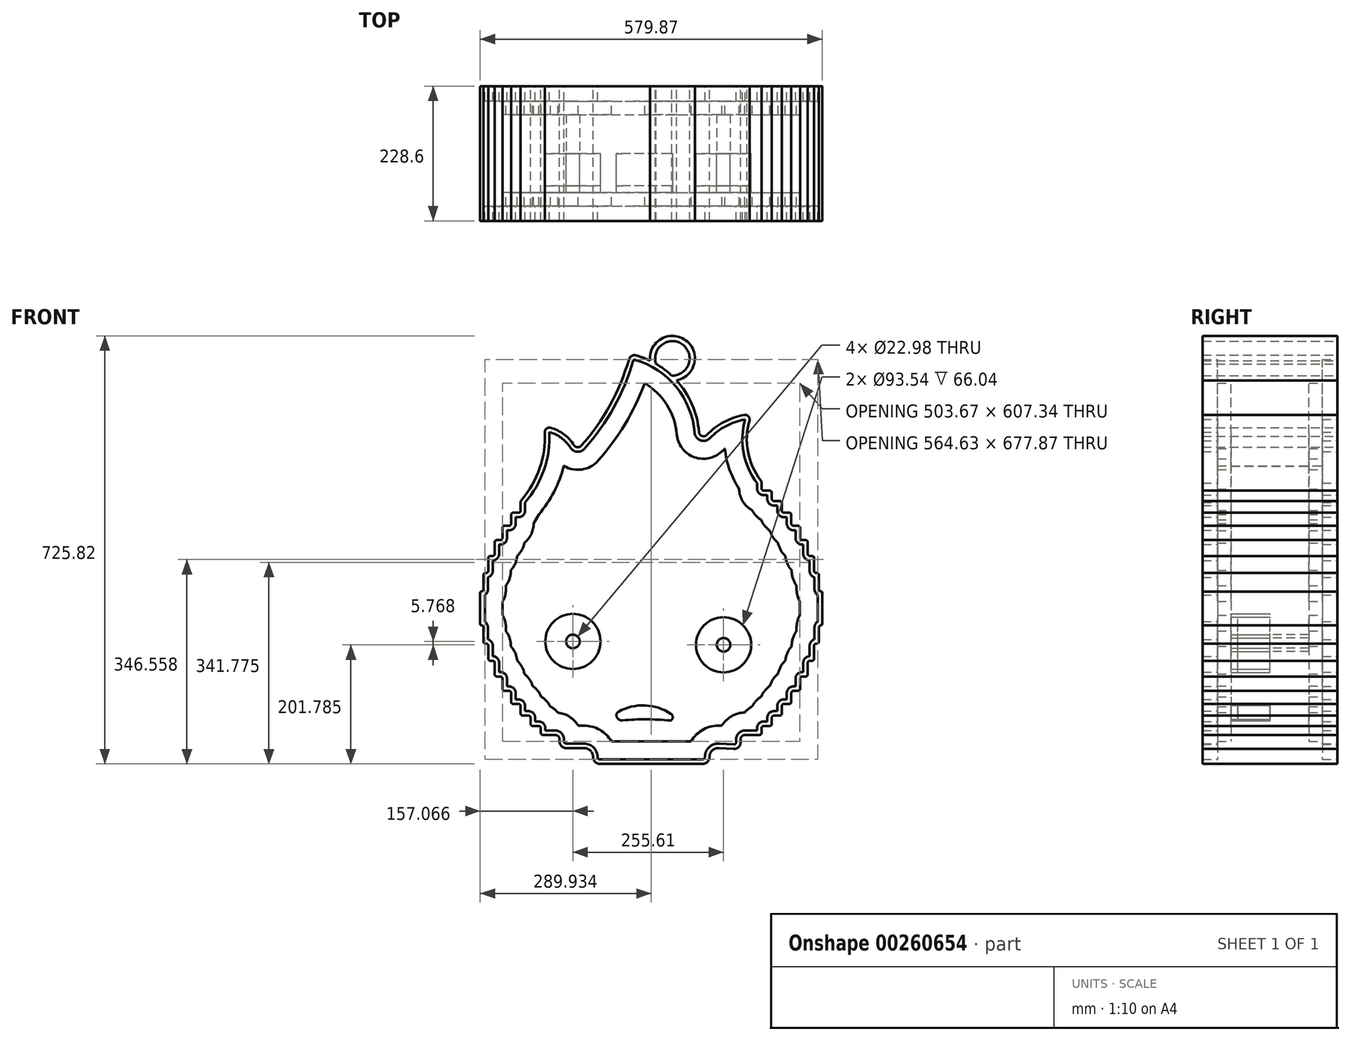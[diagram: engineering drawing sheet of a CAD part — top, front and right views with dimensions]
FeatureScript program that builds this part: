
annotation { "Feature Type Name" : "Feature", "Feature Type Description" : "" }
export const myFeature = defineFeature(function(context is Context, id is Id, definition is map)
    precondition{}
    {
        {
            var Q0;
            Q0=qCreatedBy(makeId("Front.planeOp"),FACE);
            var sketch = newSketch(context, id + "F0", { "sketchPlane" : qUnion([Q0])});
            skEllipticalArc(sketch, "E0", {});
            skArc(sketch, "E1", {"start": v(-103.1, 152.36) * mm, "mid": v(-54.44, 221.1) * mm, "end": v(-22.22, 298.9) * mm});
            skArc(sketch, "E2", {"start": v(96.67, 175.4) * mm, "mid": v(63.66, 257.18) * mm, "end": v(-10.03, 305.65) * mm});
            skPoint(sketch, "E3.visualSharp", {"position": v(-19.7, 308.07) * mm});
            skArc(sketch, "E3.filletArc", {"start": v(-10.03, 305.65) * mm, "mid": v(-17.52, 304.8) * mm, "end": v(-22.22, 298.9) * mm});
            skArc(sketch, "E4", {"start": v(-204.11, 60.77) * mm, "mid": v(-173.5, 114.23) * mm, "end": v(-164.8, 175.2) * mm});
            skArc(sketch, "E5", {"start": v(-115.23, 153.37) * mm, "mid": v(-132.43, 171.91) * mm, "end": v(-155.2, 182.92) * mm});
            skArc(sketch, "E6.filletArc", {"start": v(-115.23, 153.37) * mm, "mid": v(-109.42, 149.84) * mm, "end": v(-103.1, 152.36) * mm});
            skArc(sketch, "E7", {"start": v(173.43, 204.74) * mm, "mid": v(138.96, 192.6) * mm, "end": v(109.7, 170.68) * mm});
            skArc(sketch, "E8", {"start": v(182.17, 195.16) * mm, "mid": v(179.7, 142.05) * mm, "end": v(201.22, 93.44) * mm});
            skArc(sketch, "E9.filletArc", {"start": v(96.67, 175.4) * mm, "mid": v(101.67, 168.85) * mm, "end": v(109.7, 170.68) * mm});
            skPoint(sketch, "E10.visualSharp", {"position": v(-165.54, 184.88) * mm});
            skArc(sketch, "E10.filletArc", {"start": v(-155.2, 182.92) * mm, "mid": v(-161.96, 181.5) * mm, "end": v(-164.8, 175.2) * mm});
            skPoint(sketch, "E11.visualSharp", {"position": v(186.03, 206.44) * mm});
            skArc(sketch, "E11.filletArc", {"start": v(182.17, 195.16) * mm, "mid": v(180.47, 202.39) * mm, "end": v(173.43, 204.74) * mm});
            skLineSegment(sketch, "E12", {"start": v(202.76, 91.44) * mm, "end": v(202.3, 91.44) * mm});
            skLineSegment(sketch, "E13", {"start": v(202.76, 79.73) * mm, "end": v(202.76, 88.84) * mm});
            skLineSegment(sketch, "E14.bottom", {"start": v(-272.57, -94.8) * mm, "end": v(-272.9, -94.8) * mm});
            skLineSegment(sketch, "E14.left", {"start": v(305.47, -96.3) * mm, "end": v(305.47, -150.45) * mm});
            skLineSegment(sketch, "E14.right", {"start": v(-274.4, -96.3) * mm, "end": v(-274.4, -150.45) * mm});
            skLineSegment(sketch, "E15.bottom", {"start": v(206.3, 76.2) * mm, "end": v(216.66, 76.2) * mm});
            skLineSegment(sketch, "E15.right", {"start": v(220.19, 72.67) * mm, "end": v(220.19, 62.2) * mm});
            skLineSegment(sketch, "E16.bottom", {"start": v(223.72, 58.66) * mm, "end": v(233.63, 58.66) * mm});
            skLineSegment(sketch, "E16.left", {"start": v(-205.95, 55.8) * mm, "end": v(-205.95, 42.36) * mm});
            skLineSegment(sketch, "E16.right", {"start": v(237.16, 55.13) * mm, "end": v(237.16, 42.36) * mm});
            skLineSegment(sketch, "E17.bottom", {"start": v(-218.5, 38.83) * mm, "end": v(-209.48, 38.83) * mm});
            skLineSegment(sketch, "E17.left", {"start": v(-222.02, 35.3) * mm, "end": v(-222.02, 20.23) * mm});
            skLineSegment(sketch, "E17.right", {"start": v(253.23, 35.3) * mm, "end": v(253.23, 20.23) * mm});
            skLineSegment(sketch, "E18.bottom", {"start": v(-233.25, 16.7) * mm, "end": v(-225.55, 16.7) * mm});
            skLineSegment(sketch, "E18.left", {"start": v(-236.78, 13.17) * mm, "end": v(-236.78, -4.2) * mm});
            skLineSegment(sketch, "E18.right", {"start": v(267.99, 13.17) * mm, "end": v(267.99, -4.2) * mm});
            skLineSegment(sketch, "E19.bottom", {"start": v(-246.29, -7.73) * mm, "end": v(-240.3, -7.73) * mm});
            skLineSegment(sketch, "E19.left", {"start": v(-249.82, -11.26) * mm, "end": v(-249.82, -30.93) * mm});
            skLineSegment(sketch, "E19.right", {"start": v(281.03, -11.26) * mm, "end": v(281.03, -30.93) * mm});
            skLineSegment(sketch, "E20.bottom", {"start": v(-257.2, -34.46) * mm, "end": v(-253.34, -34.46) * mm});
            skLineSegment(sketch, "E20.left", {"start": v(-260.72, -37.98) * mm, "end": v(-260.72, -59.95) * mm});
            skLineSegment(sketch, "E20.right", {"start": v(291.93, -37.99) * mm, "end": v(291.93, -59.95) * mm});
            skLineSegment(sketch, "E21.bottom", {"start": v(-265.51, -63.48) * mm, "end": v(-264.25, -63.48) * mm});
            skLineSegment(sketch, "E21.left", {"start": v(-269.04, -67) * mm, "end": v(-269.04, -91.27) * mm});
            skLineSegment(sketch, "E21.right", {"start": v(300.26, -67) * mm, "end": v(300.26, -91.27) * mm});
            skLineSegment(sketch, "E22", {"start": v(303.97, -151.95) * mm, "end": v(300.26, -151.95) * mm});
            skLineSegment(sketch, "E23.MirrorCS", {"start": v(-272.57, -151.95) * mm, "end": v(-272.9, -151.95) * mm});
            skLineSegment(sketch, "E24.MirrorCS", {"start": v(-269.04, -183.27) * mm, "end": v(-260.72, -183.27) * mm});
            skLineSegment(sketch, "E25.MirrorCS", {"start": v(-265.51, -183.27) * mm, "end": v(-264.25, -183.27) * mm});
            skLineSegment(sketch, "E26.MirrorCS", {"start": v(-257.2, -212.3) * mm, "end": v(-253.35, -212.3) * mm});
            skLineSegment(sketch, "E27.MirrorCS", {"start": v(284.56, -212.3) * mm, "end": v(288.4, -212.3) * mm});
            skLineSegment(sketch, "E28.MirrorCS", {"start": v(271.52, -239.02) * mm, "end": v(277.5, -239.02) * mm});
            skLineSegment(sketch, "E29.MirrorCS", {"start": v(-233.25, -263.45) * mm, "end": v(-225.55, -263.45) * mm});
            skLineSegment(sketch, "E30.MirrorCS", {"start": v(-218.5, -285.58) * mm, "end": v(-209.48, -285.58) * mm});
            skLineSegment(sketch, "E31.MirrorCS", {"start": v(-202.42, -305.41) * mm, "end": v(-192.5, -305.41) * mm});
            skLineSegment(sketch, "E32.MirrorCS", {"start": v(-185.45, -322.95) * mm, "end": v(-175.08, -322.95) * mm});
            skLineSegment(sketch, "E33.MirrorCS", {"start": v(-147.5, -338.2) * mm, "end": v(-168.02, -338.2) * mm});
            skLineSegment(sketch, "E34.MirrorCS", {"start": v(-269.04, -179.74) * mm, "end": v(-269.04, -155.48) * mm});
            skLineSegment(sketch, "E35.MirrorCS", {"start": v(-260.72, -208.76) * mm, "end": v(-260.72, -186.8) * mm});
            skLineSegment(sketch, "E36.MirrorCS", {"start": v(-249.82, -235.49) * mm, "end": v(-249.82, -215.82) * mm});
            skLineSegment(sketch, "E37.MirrorCS", {"start": v(-236.78, -259.92) * mm, "end": v(-236.78, -242.55) * mm});
            skLineSegment(sketch, "E38.MirrorCS", {"start": v(-222.02, -282.05) * mm, "end": v(-222.02, -266.98) * mm});
            skLineSegment(sketch, "E39.MirrorCS", {"start": v(-205.95, -301.88) * mm, "end": v(-205.95, -289.1) * mm});
            skLineSegment(sketch, "E40.MirrorCS", {"start": v(-188.98, -319.42) * mm, "end": v(-188.98, -308.94) * mm});
            skLineSegment(sketch, "E41.MirrorCS", {"start": v(-171.55, -334.66) * mm, "end": v(-171.55, -326.48) * mm});
            skLineSegment(sketch, "E42.MirrorCS", {"start": v(202.76, -326.48) * mm, "end": v(202.76, -334.66) * mm});
            skLineSegment(sketch, "E43.MirrorCS", {"start": v(220.19, -319.42) * mm, "end": v(220.19, -308.94) * mm});
            skLineSegment(sketch, "E44.MirrorCS", {"start": v(237.16, -301.88) * mm, "end": v(237.16, -289.1) * mm});
            skLineSegment(sketch, "E45.MirrorCS", {"start": v(253.23, -282.05) * mm, "end": v(253.23, -266.98) * mm});
            skLineSegment(sketch, "E46.MirrorCS", {"start": v(267.99, -259.92) * mm, "end": v(267.99, -242.55) * mm});
            skLineSegment(sketch, "E47.MirrorCS", {"start": v(281.03, -235.49) * mm, "end": v(281.03, -215.82) * mm});
            skLineSegment(sketch, "E48.MirrorCS", {"start": v(291.93, -208.76) * mm, "end": v(291.93, -186.8) * mm});
            skLineSegment(sketch, "E49.MirrorCS", {"start": v(300.26, -179.74) * mm, "end": v(300.26, -155.48) * mm});
            skLineSegment(sketch, "E50.top", {"start": v(-128.44, -360.42) * mm, "end": v(-98.32, -360.42) * mm});
            skLineSegment(sketch, "E50.left", {"start": v(-139.87, -345.81) * mm, "end": v(-139.87, -348.99) * mm});
            skLineSegment(sketch, "E50.right", {"start": v(167.2, -345.81) * mm, "end": v(167.2, -350.57) * mm});
            skPoint(sketch, "E51.newPointA", {"position": v(-205.95, 38.83) * mm});
            skPoint(sketch, "E51.newPointB", {"position": v(253.23, 38.83) * mm});
            skArc(sketch, "E51.filletArc", {"start": v(-209.48, 38.83) * mm, "mid": v(-206.98, 39.86) * mm, "end": v(-205.95, 42.36) * mm});
            skPoint(sketch, "E52.visualSharp", {"position": v(-222.02, 38.83) * mm});
            skArc(sketch, "E52.filletArc", {"start": v(-218.5, 38.83) * mm, "mid": v(-220.99, 37.8) * mm, "end": v(-222.02, 35.3) * mm});
            skPoint(sketch, "E53.newPointA", {"position": v(281.03, -7.73) * mm});
            skPoint(sketch, "E53.newPointB", {"position": v(-236.78, -7.73) * mm});
            skArc(sketch, "E53.filletArc", {"start": v(-240.3, -7.73) * mm, "mid": v(-237.8, -6.7) * mm, "end": v(-236.78, -4.2) * mm});
            skPoint(sketch, "E54.visualSharp", {"position": v(-236.78, 16.7) * mm});
            skArc(sketch, "E54.filletArc", {"start": v(-233.25, 16.7) * mm, "mid": v(-235.74, 15.67) * mm, "end": v(-236.78, 13.17) * mm});
            skPoint(sketch, "E55.newPointA", {"position": v(-222.02, 16.7) * mm});
            skPoint(sketch, "E55.newPointB", {"position": v(267.99, 16.7) * mm});
            skArc(sketch, "E55.filletArc", {"start": v(-225.55, 16.7) * mm, "mid": v(-223.05, 17.73) * mm, "end": v(-222.02, 20.23) * mm});
            skPoint(sketch, "E56.visualSharp", {"position": v(-249.82, -7.73) * mm});
            skArc(sketch, "E56.filletArc", {"start": v(-246.29, -7.73) * mm, "mid": v(-248.78, -8.76) * mm, "end": v(-249.82, -11.26) * mm});
            skPoint(sketch, "E57.newPointA", {"position": v(291.93, -34.46) * mm});
            skPoint(sketch, "E57.newPointB", {"position": v(-249.82, -34.46) * mm});
            skArc(sketch, "E57.filletArc", {"start": v(-253.34, -34.46) * mm, "mid": v(-250.85, -33.42) * mm, "end": v(-249.82, -30.93) * mm});
            skPoint(sketch, "E58.visualSharp", {"position": v(-205.95, 58.66) * mm});
            skArc(sketch, "E58.filletArc", {"start": v(-204.11, 60.77) * mm, "mid": v(-205.48, 58.45) * mm, "end": v(-205.95, 55.8) * mm});
            skPoint(sketch, "E59.visualSharp", {"position": v(-260.72, -34.46) * mm});
            skArc(sketch, "E59.filletArc", {"start": v(-257.2, -34.46) * mm, "mid": v(-259.69, -35.49) * mm, "end": v(-260.72, -37.98) * mm});
            skPoint(sketch, "E60.visualSharp", {"position": v(-269.04, -63.48) * mm});
            skArc(sketch, "E60.filletArc", {"start": v(-265.51, -63.48) * mm, "mid": v(-268, -64.51) * mm, "end": v(-269.04, -67) * mm});
            skPoint(sketch, "E61.newPointA", {"position": v(300.26, -63.48) * mm});
            skArc(sketch, "E61.filletArc", {"start": v(-264.25, -63.48) * mm, "mid": v(-261.76, -62.44) * mm, "end": v(-260.72, -59.95) * mm});
            skPoint(sketch, "E62.newPointA", {"position": v(305.61, -94.8) * mm});
            skPoint(sketch, "E62.newPointB", {"position": v(-269.04, -94.8) * mm});
            skArc(sketch, "E62.filletArc", {"start": v(-272.57, -94.8) * mm, "mid": v(-270.08, -93.77) * mm, "end": v(-269.04, -91.27) * mm});
            skPoint(sketch, "E63.visualSharp", {"position": v(-274.4, -94.8) * mm});
            skArc(sketch, "E63.filletArc", {"start": v(-272.9, -94.8) * mm, "mid": v(-273.96, -95.24) * mm, "end": v(-274.4, -96.3) * mm});
            skPoint(sketch, "E64.newPointA", {"position": v(305.61, -151.95) * mm});
            skPoint(sketch, "E64.newPointB", {"position": v(-269.04, -151.95) * mm});
            skArc(sketch, "E64.filletArc", {"start": v(-269.04, -155.48) * mm, "mid": v(-270.08, -152.98) * mm, "end": v(-272.57, -151.95) * mm});
            skPoint(sketch, "E65.visualSharp", {"position": v(-274.4, -151.95) * mm});
            skArc(sketch, "E65.filletArc", {"start": v(-274.4, -150.45) * mm, "mid": v(-273.96, -151.51) * mm, "end": v(-272.9, -151.95) * mm});
            skPoint(sketch, "E66.newPointA", {"position": v(300.26, -183.27) * mm});
            skPoint(sketch, "E66.newPointB", {"position": v(-260.72, -183.27) * mm});
            skArc(sketch, "E66.filletArc", {"start": v(-260.72, -186.8) * mm, "mid": v(-261.76, -184.3) * mm, "end": v(-264.25, -183.27) * mm});
            skPoint(sketch, "E67.visualSharp", {"position": v(-269.04, -183.27) * mm});
            skArc(sketch, "E67.filletArc", {"start": v(-269.04, -179.74) * mm, "mid": v(-268, -182.24) * mm, "end": v(-265.51, -183.27) * mm});
            skPoint(sketch, "E68.visualSharp", {"position": v(-260.72, -212.3) * mm});
            skArc(sketch, "E68.filletArc", {"start": v(-260.72, -208.76) * mm, "mid": v(-259.69, -211.26) * mm, "end": v(-257.2, -212.3) * mm});
            skPoint(sketch, "E69.visualSharp", {"position": v(-249.82, -239.02) * mm});
            skArc(sketch, "E69.filletArc", {"start": v(-249.82, -235.49) * mm, "mid": v(-248.78, -237.98) * mm, "end": v(-246.28, -239.02) * mm});
            skPoint(sketch, "E70.visualSharp", {"position": v(-236.78, -263.45) * mm});
            skArc(sketch, "E70.filletArc", {"start": v(-236.78, -259.92) * mm, "mid": v(-235.74, -262.41) * mm, "end": v(-233.25, -263.45) * mm});
            skPoint(sketch, "E71.visualSharp", {"position": v(-222.02, -285.58) * mm});
            skArc(sketch, "E71.filletArc", {"start": v(-222.02, -282.05) * mm, "mid": v(-220.99, -284.54) * mm, "end": v(-218.5, -285.58) * mm});
            skPoint(sketch, "E72.visualSharp", {"position": v(-205.95, -305.41) * mm});
            skArc(sketch, "E72.filletArc", {"start": v(-205.95, -301.88) * mm, "mid": v(-204.92, -304.38) * mm, "end": v(-202.42, -305.41) * mm});
            skPoint(sketch, "E73.visualSharp", {"position": v(-188.98, -322.95) * mm});
            skArc(sketch, "E73.filletArc", {"start": v(-188.98, -319.42) * mm, "mid": v(-187.94, -321.92) * mm, "end": v(-185.45, -322.95) * mm});
            skPoint(sketch, "E74.visualSharp", {"position": v(-171.55, -338.2) * mm});
            skArc(sketch, "E74.filletArc", {"start": v(-171.55, -334.66) * mm, "mid": v(-170.52, -337.16) * mm, "end": v(-168.02, -338.2) * mm});
            skLineSegment(sketch, "E75", {"start": v(240.7, 38.83) * mm, "end": v(249.7, 38.83) * mm});
            skLineSegment(sketch, "E76", {"start": v(256.76, 16.7) * mm, "end": v(264.46, 16.7) * mm});
            skLineSegment(sketch, "E77", {"start": v(271.52, -7.73) * mm, "end": v(277.5, -7.73) * mm});
            skLineSegment(sketch, "E78", {"start": v(284.56, -34.46) * mm, "end": v(288.4, -34.46) * mm});
            skLineSegment(sketch, "E79", {"start": v(295.47, -63.48) * mm, "end": v(296.73, -63.48) * mm});
            skLineSegment(sketch, "E80", {"start": v(303.79, -94.8) * mm, "end": v(303.97, -94.8) * mm});
            skLineSegment(sketch, "E81.MirrorCS", {"start": v(240.7, -285.58) * mm, "end": v(249.7, -285.58) * mm});
            skLineSegment(sketch, "E82.MirrorCS", {"start": v(256.76, -263.45) * mm, "end": v(264.46, -263.45) * mm});
            skLineSegment(sketch, "E83.MirrorCS", {"start": v(295.47, -183.27) * mm, "end": v(296.73, -183.27) * mm});
            skLineSegment(sketch, "E84.MirrorCS", {"start": v(303.79, -151.95) * mm, "end": v(303.97, -151.95) * mm});
            skPoint(sketch, "E85.visualSharp", {"position": v(202.76, 91.44) * mm});
            skArc(sketch, "E85.filletArc", {"start": v(202.76, 88.84) * mm, "mid": v(202.37, 91.26) * mm, "end": v(201.22, 93.44) * mm});
            skPoint(sketch, "E86.newPointA", {"position": v(202.76, 76.2) * mm});
            skPoint(sketch, "E86.newPointB", {"position": v(-188.98, 76.2) * mm});
            skArc(sketch, "E86.filletArc", {"start": v(202.76, 79.73) * mm, "mid": v(203.8, 77.24) * mm, "end": v(206.3, 76.2) * mm});
            skPoint(sketch, "E87.visualSharp", {"position": v(220.19, 76.2) * mm});
            skArc(sketch, "E87.filletArc", {"start": v(220.19, 72.67) * mm, "mid": v(219.15, 75.17) * mm, "end": v(216.66, 76.2) * mm});
            skPoint(sketch, "E88.newPointA", {"position": v(220.19, 58.66) * mm});
            skArc(sketch, "E88.filletArc", {"start": v(220.19, 62.2) * mm, "mid": v(221.22, 59.7) * mm, "end": v(223.72, 58.66) * mm});
            skPoint(sketch, "E89.visualSharp", {"position": v(237.16, 58.66) * mm});
            skArc(sketch, "E89.filletArc", {"start": v(237.16, 55.13) * mm, "mid": v(236.13, 57.63) * mm, "end": v(233.63, 58.66) * mm});
            skPoint(sketch, "E90.visualSharp", {"position": v(237.16, 38.83) * mm});
            skArc(sketch, "E90.filletArc", {"start": v(237.16, 42.36) * mm, "mid": v(238.2, 39.86) * mm, "end": v(240.7, 38.83) * mm});
            skArc(sketch, "E91.filletArc", {"start": v(253.23, 35.3) * mm, "mid": v(252.2, 37.8) * mm, "end": v(249.7, 38.83) * mm});
            skPoint(sketch, "E92.visualSharp", {"position": v(253.23, 16.7) * mm});
            skArc(sketch, "E92.filletArc", {"start": v(253.23, 20.23) * mm, "mid": v(254.27, 17.73) * mm, "end": v(256.76, 16.7) * mm});
            skArc(sketch, "E93.filletArc", {"start": v(267.99, 13.17) * mm, "mid": v(266.95, 15.66) * mm, "end": v(264.46, 16.7) * mm});
            skPoint(sketch, "E94.visualSharp", {"position": v(267.99, -7.73) * mm});
            skArc(sketch, "E94.filletArc", {"start": v(267.99, -4.2) * mm, "mid": v(269.02, -6.7) * mm, "end": v(271.52, -7.73) * mm});
            skArc(sketch, "E95.filletArc", {"start": v(281.03, -11.26) * mm, "mid": v(280, -8.76) * mm, "end": v(277.5, -7.73) * mm});
            skPoint(sketch, "E96.visualSharp", {"position": v(281.03, -34.46) * mm});
            skArc(sketch, "E96.filletArc", {"start": v(281.03, -30.93) * mm, "mid": v(282.06, -33.42) * mm, "end": v(284.56, -34.46) * mm});
            skArc(sketch, "E97.filletArc", {"start": v(291.93, -37.99) * mm, "mid": v(290.9, -35.5) * mm, "end": v(288.4, -34.46) * mm});
            skPoint(sketch, "E98.visualSharp", {"position": v(291.93, -63.48) * mm});
            skArc(sketch, "E98.filletArc", {"start": v(291.93, -59.95) * mm, "mid": v(292.97, -62.44) * mm, "end": v(295.47, -63.48) * mm});
            skArc(sketch, "E99.filletArc", {"start": v(300.26, -67) * mm, "mid": v(299.22, -64.51) * mm, "end": v(296.73, -63.48) * mm});
            skPoint(sketch, "E100.visualSharp", {"position": v(300.26, -94.8) * mm});
            skArc(sketch, "E100.filletArc", {"start": v(300.26, -91.27) * mm, "mid": v(301.29, -93.77) * mm, "end": v(303.79, -94.8) * mm});
            skPoint(sketch, "E101.visualSharp", {"position": v(305.47, -94.8) * mm});
            skArc(sketch, "E101.filletArc", {"start": v(305.47, -96.3) * mm, "mid": v(305.03, -95.24) * mm, "end": v(303.97, -94.8) * mm});
            skPoint(sketch, "E102.visualSharp", {"position": v(305.47, -151.95) * mm});
            skArc(sketch, "E102.filletArc", {"start": v(303.97, -151.95) * mm, "mid": v(305.03, -151.51) * mm, "end": v(305.47, -150.45) * mm});
            skPoint(sketch, "E103.visualSharp", {"position": v(300.26, -151.95) * mm});
            skArc(sketch, "E103.filletArc", {"start": v(303.79, -151.95) * mm, "mid": v(301.29, -152.98) * mm, "end": v(300.26, -155.48) * mm});
            skArc(sketch, "E104.filletArc", {"start": v(296.73, -183.27) * mm, "mid": v(299.22, -182.24) * mm, "end": v(300.26, -179.74) * mm});
            skPoint(sketch, "E105.visualSharp", {"position": v(291.93, -183.27) * mm});
            skArc(sketch, "E105.filletArc", {"start": v(295.47, -183.27) * mm, "mid": v(292.97, -184.3) * mm, "end": v(291.93, -186.8) * mm});
            skLineSegment(sketch, "E106.trimOffspring", {"start": v(-274.26, -151.95) * mm, "end": v(-274.4, -151.95) * mm});
            skPoint(sketch, "E107.visualSharp", {"position": v(291.93, -212.3) * mm});
            skArc(sketch, "E107.filletArc", {"start": v(288.4, -212.3) * mm, "mid": v(290.9, -211.26) * mm, "end": v(291.93, -208.76) * mm});
            skPoint(sketch, "E108.newPointA", {"position": v(281.03, -212.3) * mm});
            skArc(sketch, "E108.filletArc", {"start": v(284.56, -212.3) * mm, "mid": v(282.06, -213.33) * mm, "end": v(281.03, -215.82) * mm});
            skPoint(sketch, "E109.visualSharp", {"position": v(281.03, -239.02) * mm});
            skArc(sketch, "E109.filletArc", {"start": v(277.5, -239.02) * mm, "mid": v(280, -237.98) * mm, "end": v(281.03, -235.49) * mm});
            skPoint(sketch, "E110.newPointA", {"position": v(267.99, -239.02) * mm});
            skArc(sketch, "E110.filletArc", {"start": v(271.52, -239.02) * mm, "mid": v(269.02, -240.05) * mm, "end": v(267.99, -242.55) * mm});
            skLineSegment(sketch, "E111", {"start": v(-246.28, -239.02) * mm, "end": v(-240.3, -239.02) * mm});
            skPoint(sketch, "E112.newPointB", {"position": v(-249.82, -212.3) * mm});
            skArc(sketch, "E112.filletArc", {"start": v(-249.82, -215.82) * mm, "mid": v(-250.85, -213.33) * mm, "end": v(-253.35, -212.3) * mm});
            skPoint(sketch, "E113.visualSharp", {"position": v(-236.78, -239.02) * mm});
            skArc(sketch, "E113.filletArc", {"start": v(-236.78, -242.55) * mm, "mid": v(-237.81, -240.05) * mm, "end": v(-240.3, -239.02) * mm});
            skPoint(sketch, "E114.newPointA", {"position": v(267.99, -263.45) * mm});
            skPoint(sketch, "E114.newPointB", {"position": v(-222.02, -263.45) * mm});
            skArc(sketch, "E114.filletArc", {"start": v(-222.02, -266.98) * mm, "mid": v(-223.05, -264.48) * mm, "end": v(-225.55, -263.45) * mm});
            skPoint(sketch, "E115.newPointA", {"position": v(253.23, -285.58) * mm});
            skPoint(sketch, "E115.newPointB", {"position": v(-205.95, -285.58) * mm});
            skArc(sketch, "E115.filletArc", {"start": v(-205.95, -289.1) * mm, "mid": v(-206.98, -286.61) * mm, "end": v(-209.48, -285.58) * mm});
            skPoint(sketch, "E116.newPointA", {"position": v(237.16, -305.41) * mm});
            skPoint(sketch, "E116.newPointB", {"position": v(-188.98, -305.41) * mm});
            skArc(sketch, "E116.filletArc", {"start": v(-188.98, -308.94) * mm, "mid": v(-190, -306.45) * mm, "end": v(-192.5, -305.41) * mm});
            skPoint(sketch, "E117.newPointA", {"position": v(220.19, -322.95) * mm});
            skPoint(sketch, "E117.newPointB", {"position": v(-171.55, -322.95) * mm});
            skArc(sketch, "E117.filletArc", {"start": v(-171.55, -326.48) * mm, "mid": v(-172.59, -323.98) * mm, "end": v(-175.08, -322.95) * mm});
            skLineSegment(sketch, "E118", {"start": v(206.3, -322.95) * mm, "end": v(216.66, -322.95) * mm});
            skLineSegment(sketch, "E119", {"start": v(223.72, -305.41) * mm, "end": v(233.63, -305.41) * mm});
            skArc(sketch, "E120.filletArc", {"start": v(264.46, -263.45) * mm, "mid": v(266.95, -262.41) * mm, "end": v(267.99, -259.92) * mm});
            skPoint(sketch, "E121.visualSharp", {"position": v(253.23, -263.45) * mm});
            skArc(sketch, "E121.filletArc", {"start": v(256.76, -263.45) * mm, "mid": v(254.27, -264.48) * mm, "end": v(253.23, -266.98) * mm});
            skArc(sketch, "E122.filletArc", {"start": v(249.7, -285.58) * mm, "mid": v(252.2, -284.54) * mm, "end": v(253.23, -282.05) * mm});
            skPoint(sketch, "E123.visualSharp", {"position": v(237.16, -285.58) * mm});
            skArc(sketch, "E123.filletArc", {"start": v(240.7, -285.58) * mm, "mid": v(238.2, -286.61) * mm, "end": v(237.16, -289.1) * mm});
            skArc(sketch, "E124.filletArc", {"start": v(233.63, -305.41) * mm, "mid": v(236.13, -304.38) * mm, "end": v(237.16, -301.88) * mm});
            skPoint(sketch, "E125.visualSharp", {"position": v(220.19, -305.41) * mm});
            skArc(sketch, "E125.filletArc", {"start": v(223.72, -305.41) * mm, "mid": v(221.22, -306.45) * mm, "end": v(220.19, -308.94) * mm});
            skPoint(sketch, "E126.visualSharp", {"position": v(202.76, -322.95) * mm});
            skArc(sketch, "E126.filletArc", {"start": v(206.3, -322.95) * mm, "mid": v(203.8, -323.98) * mm, "end": v(202.76, -326.48) * mm});
            skArc(sketch, "E127.filletArc", {"start": v(216.66, -322.95) * mm, "mid": v(219.15, -321.92) * mm, "end": v(220.19, -319.42) * mm});
            skPoint(sketch, "E128.visualSharp", {"position": v(202.76, -338.2) * mm});
            skArc(sketch, "E128.filletArc", {"start": v(199.23, -338.2) * mm, "mid": v(201.73, -337.16) * mm, "end": v(202.76, -334.66) * mm});
            skLineSegment(sketch, "E129.top", {"start": v(-71.65, -387.09) * mm, "end": v(102.87, -387.09) * mm});
            skLineSegment(sketch, "E129.left", {"start": v(-83.08, -375.66) * mm, "end": v(-83.08, -375.66) * mm});
            skLineSegment(sketch, "E129.right", {"start": v(114.3, -375.66) * mm, "end": v(114.3, -375.66) * mm});
            skArc(sketch, "E130.filletArc", {"start": v(-139.87, -345.81) * mm, "mid": v(-142.1, -340.42) * mm, "end": v(-147.5, -338.2) * mm});
            skPoint(sketch, "E131.visualSharp", {"position": v(-139.87, -360.42) * mm});
            skArc(sketch, "E131.filletArc", {"start": v(-139.87, -348.99) * mm, "mid": v(-136.53, -357.07) * mm, "end": v(-128.44, -360.42) * mm});
            skArc(sketch, "E132.filletArc", {"start": v(-83.08, -375.66) * mm, "mid": v(-87.55, -364.88) * mm, "end": v(-98.32, -360.42) * mm});
            skPoint(sketch, "E133.visualSharp", {"position": v(-83.08, -387.09) * mm});
            skArc(sketch, "E133.filletArc", {"start": v(-83.08, -375.66) * mm, "mid": v(-79.74, -383.74) * mm, "end": v(-71.65, -387.09) * mm});
            skPoint(sketch, "E134.visualSharp", {"position": v(114.3, -387.09) * mm});
            skArc(sketch, "E134.filletArc", {"start": v(102.87, -387.09) * mm, "mid": v(110.95, -383.74) * mm, "end": v(114.3, -375.66) * mm});
            skLineSegment(sketch, "E135", {"start": v(130.48, -360.45) * mm, "end": v(155.07, -361.97) * mm});
            skPoint(sketch, "E136.visualSharp", {"position": v(114.3, -359.44) * mm});
            skArc(sketch, "E136.filletArc", {"start": v(130.48, -360.45) * mm, "mid": v(119.1, -364.55) * mm, "end": v(114.3, -375.66) * mm});
            skLineSegment(sketch, "E137", {"start": v(174.83, -338.2) * mm, "end": v(199.23, -338.2) * mm});
            skPoint(sketch, "E138.visualSharp", {"position": v(167.2, -362.73) * mm});
            skArc(sketch, "E138.filletArc", {"start": v(155.07, -361.97) * mm, "mid": v(163.6, -358.9) * mm, "end": v(167.2, -350.57) * mm});
            skPoint(sketch, "E139.visualSharp", {"position": v(167.2, -338.2) * mm});
            skArc(sketch, "E139.filletArc", {"start": v(174.83, -338.2) * mm, "mid": v(169.44, -340.42) * mm, "end": v(167.2, -345.81) * mm});
            skLineSegment(sketch, "E140.trimOffspring", {"start": v(291.93, -183.27) * mm, "end": v(296.73, -183.27) * mm});
            skLineSegment(sketch, "E141.trimOffspring", {"start": v(-269.04, -151.95) * mm, "end": v(-272.9, -151.95) * mm});
            skPoint(sketch, "E142.orphan", {"position": v(305.47, -123.37) * mm});
            skPoint(sketch, "E143.start.orphan", {"position": v(-274.4, -123.37) * mm});
            skLineSegment(sketch, "E144.0", {"start": v(284.31, -208.76) * mm, "end": v(284.31, -186.8) * mm});
            skArc(sketch, "E144.1", {"start": v(292.64, -176.02) * mm, "mid": v(286.64, -180) * mm, "end": v(284.31, -186.8) * mm});
            skLineSegment(sketch, "E144.2", {"start": v(292.64, -176.02) * mm, "end": v(292.64, -155.48) * mm});
            skArc(sketch, "E144.3", {"start": v(297.85, -146.04) * mm, "mid": v(294.03, -150.09) * mm, "end": v(292.64, -155.48) * mm});
            skLineSegment(sketch, "E144.4", {"start": v(297.85, -100.7) * mm, "end": v(297.85, -146.04) * mm});
            skArc(sketch, "E144.5", {"start": v(292.64, -91.27) * mm, "mid": v(294.03, -96.66) * mm, "end": v(297.85, -100.7) * mm});
            skLineSegment(sketch, "E144.6", {"start": v(292.64, -70.73) * mm, "end": v(292.64, -91.27) * mm});
            skArc(sketch, "E144.7", {"start": v(284.31, -59.95) * mm, "mid": v(286.64, -66.76) * mm, "end": v(292.64, -70.73) * mm});
            skLineSegment(sketch, "E144.8", {"start": v(284.31, -42.08) * mm, "end": v(284.31, -59.95) * mm});
            skLineSegment(sketch, "E144.9", {"start": v(284.31, -42.08) * mm, "end": v(284.56, -42.08) * mm});
            skArc(sketch, "E144.10", {"start": v(273.4, -30.93) * mm, "mid": v(276.67, -38.81) * mm, "end": v(284.56, -42.08) * mm});
            skLineSegment(sketch, "E144.11", {"start": v(273.4, -15.35) * mm, "end": v(273.4, -30.93) * mm});
            skLineSegment(sketch, "E144.12", {"start": v(271.52, -15.35) * mm, "end": v(273.4, -15.35) * mm});
            skArc(sketch, "E144.13", {"start": v(260.37, -4.2) * mm, "mid": v(263.63, -12.08) * mm, "end": v(271.52, -15.35) * mm});
            skLineSegment(sketch, "E144.14", {"start": v(260.37, 9.08) * mm, "end": v(260.37, -4.2) * mm});
            skLineSegment(sketch, "E144.15", {"start": v(256.76, 9.08) * mm, "end": v(260.37, 9.08) * mm});
            skArc(sketch, "E144.16", {"start": v(245.61, 20.23) * mm, "mid": v(248.88, 12.34) * mm, "end": v(256.76, 9.08) * mm});
            skLineSegment(sketch, "E144.17", {"start": v(174.84, 197.25) * mm, "end": v(174.84, 197.25) * mm});
            skArc(sketch, "E144.18", {"start": v(174.84, 197.25) * mm, "mid": v(142.55, 185.87) * mm, "end": v(115.14, 165.35) * mm});
            skArc(sketch, "E144.19", {"start": v(89.07, 174.79) * mm, "mid": v(99.07, 161.7) * mm, "end": v(115.14, 165.35) * mm});
            skArc(sketch, "E144.20", {"start": v(89.07, 174.79) * mm, "mid": v(57.76, 252.36) * mm, "end": v(-12.13, 298.32) * mm});
            skArc(sketch, "E144.21", {"start": v(-12.13, 298.32) * mm, "mid": v(-13.83, 298.13) * mm, "end": v(-14.9, 296.79) * mm});
            skArc(sketch, "E144.22", {"start": v(-97.4, 147.3) * mm, "mid": v(-47.77, 217.42) * mm, "end": v(-14.9, 296.79) * mm});
            skArc(sketch, "E144.23", {"start": v(-198.33, 55.8) * mm, "mid": v(-166.3, 111.75) * mm, "end": v(-157.19, 175.57) * mm});
            skLineSegment(sketch, "E144.24", {"start": v(-157.19, 175.57) * mm, "end": v(-157.19, 175.57) * mm});
            skArc(sketch, "E144.25", {"start": v(-121.68, 149.32) * mm, "mid": v(-136.96, 165.79) * mm, "end": v(-157.19, 175.57) * mm});
            skArc(sketch, "E144.26", {"start": v(-121.68, 149.32) * mm, "mid": v(-110.05, 142.24) * mm, "end": v(-97.4, 147.3) * mm});
            skArc(sketch, "E144.27", {"start": v(174.84, 197.25) * mm, "mid": v(172.2, 140.65) * mm, "end": v(195.14, 88.84) * mm});
            skLineSegment(sketch, "E144.28", {"start": v(195.14, 88.84) * mm, "end": v(195.14, 88.84) * mm});
            skLineSegment(sketch, "E144.29", {"start": v(195.14, 79.73) * mm, "end": v(195.14, 88.84) * mm});
            skArc(sketch, "E144.30", {"start": v(195.14, 79.73) * mm, "mid": v(198.41, 71.85) * mm, "end": v(206.3, 68.58) * mm});
            skLineSegment(sketch, "E144.31", {"start": v(206.3, 68.58) * mm, "end": v(212.57, 68.58) * mm});
            skLineSegment(sketch, "E144.32", {"start": v(212.57, 68.58) * mm, "end": v(212.57, 62.2) * mm});
            skArc(sketch, "E144.33", {"start": v(212.57, 62.2) * mm, "mid": v(215.83, 54.31) * mm, "end": v(223.72, 51.04) * mm});
            skLineSegment(sketch, "E144.34", {"start": v(223.72, 51.04) * mm, "end": v(229.54, 51.04) * mm});
            skLineSegment(sketch, "E144.35", {"start": v(229.54, 51.04) * mm, "end": v(229.54, 42.36) * mm});
            skArc(sketch, "E144.36", {"start": v(229.54, 42.36) * mm, "mid": v(232.8, 34.48) * mm, "end": v(240.7, 31.21) * mm});
            skLineSegment(sketch, "E144.37", {"start": v(240.7, 31.21) * mm, "end": v(245.61, 31.21) * mm});
            skLineSegment(sketch, "E144.38", {"start": v(245.61, 31.21) * mm, "end": v(245.61, 20.23) * mm});
            skArc(sketch, "E145.0", {"start": v(206.3, -315.33) * mm, "mid": v(198.41, -318.6) * mm, "end": v(195.14, -326.48) * mm});
            skLineSegment(sketch, "E145.1", {"start": v(206.3, -315.33) * mm, "end": v(212.57, -315.33) * mm});
            skLineSegment(sketch, "E145.2", {"start": v(212.57, -315.33) * mm, "end": v(212.57, -308.94) * mm});
            skArc(sketch, "E145.3", {"start": v(223.72, -297.8) * mm, "mid": v(215.83, -301.06) * mm, "end": v(212.57, -308.94) * mm});
            skLineSegment(sketch, "E145.4", {"start": v(223.72, -297.8) * mm, "end": v(229.54, -297.8) * mm});
            skLineSegment(sketch, "E145.5", {"start": v(229.54, -297.8) * mm, "end": v(229.54, -289.1) * mm});
            skArc(sketch, "E145.6", {"start": v(240.7, -277.96) * mm, "mid": v(232.8, -281.22) * mm, "end": v(229.54, -289.1) * mm});
            skLineSegment(sketch, "E145.7", {"start": v(271.52, -231.4) * mm, "end": v(273.4, -231.4) * mm});
            skLineSegment(sketch, "E145.8", {"start": v(273.4, -231.4) * mm, "end": v(273.4, -215.82) * mm});
            skArc(sketch, "E145.9", {"start": v(284.31, -204.68) * mm, "mid": v(276.59, -208.03) * mm, "end": v(273.4, -215.82) * mm});
            skLineSegment(sketch, "E145.10", {"start": v(284.31, -204.68) * mm, "end": v(284.31, -186.8) * mm});
            skArc(sketch, "E145.11", {"start": v(271.52, -231.4) * mm, "mid": v(263.63, -234.66) * mm, "end": v(260.37, -242.55) * mm});
            skLineSegment(sketch, "E145.12", {"start": v(260.37, -255.83) * mm, "end": v(260.37, -242.55) * mm});
            skLineSegment(sketch, "E145.13", {"start": v(256.76, -255.83) * mm, "end": v(260.37, -255.83) * mm});
            skArc(sketch, "E145.14", {"start": v(256.76, -255.83) * mm, "mid": v(248.88, -259.1) * mm, "end": v(245.61, -266.98) * mm});
            skLineSegment(sketch, "E145.15", {"start": v(245.61, -277.96) * mm, "end": v(245.61, -266.98) * mm});
            skLineSegment(sketch, "E145.16", {"start": v(240.7, -277.96) * mm, "end": v(245.61, -277.96) * mm});
            skLineSegment(sketch, "E146.0", {"start": v(130.01, -352.78) * mm, "end": v(155.54, -354.37) * mm});
            skArc(sketch, "E146.1", {"start": v(155.54, -354.37) * mm, "mid": v(158.39, -353.34) * mm, "end": v(159.59, -350.57) * mm});
            skLineSegment(sketch, "E146.2", {"start": v(195.14, -326.48) * mm, "end": v(195.14, -330.57) * mm});
            skLineSegment(sketch, "E146.3", {"start": v(174.83, -330.57) * mm, "end": v(195.14, -330.57) * mm});
            skArc(sketch, "E146.4", {"start": v(174.83, -330.57) * mm, "mid": v(164.05, -335.03) * mm, "end": v(159.59, -345.81) * mm});
            skLineSegment(sketch, "E146.5", {"start": v(159.59, -345.81) * mm, "end": v(159.59, -350.57) * mm});
            skArc(sketch, "E147.0", {"start": v(102.87, -379.47) * mm, "mid": v(105.56, -378.35) * mm, "end": v(106.68, -375.66) * mm});
            skArc(sketch, "E147.1", {"start": v(130.96, -352.84) * mm, "mid": v(113.88, -359) * mm, "end": v(106.68, -375.66) * mm});
            skLineSegment(sketch, "E147.2", {"start": v(130.96, -352.84) * mm, "end": v(155.54, -354.37) * mm});
            skLineSegment(sketch, "E148.0", {"start": v(-71.65, -379.47) * mm, "end": v(102.87, -379.47) * mm});
            skArc(sketch, "E148.1", {"start": v(-75.46, -375.66) * mm, "mid": v(-74.35, -378.35) * mm, "end": v(-71.65, -379.47) * mm});
            skArc(sketch, "E148.2", {"start": v(-75.46, -375.66) * mm, "mid": v(-82.16, -359.5) * mm, "end": v(-98.32, -352.8) * mm});
            skArc(sketch, "E148.3", {"start": v(-198.33, -289.1) * mm, "mid": v(-201.6, -281.22) * mm, "end": v(-209.48, -277.96) * mm});
            skLineSegment(sketch, "E148.4", {"start": v(-214.4, -277.96) * mm, "end": v(-209.48, -277.96) * mm});
            skLineSegment(sketch, "E148.5", {"start": v(-214.4, -277.96) * mm, "end": v(-214.4, -266.98) * mm});
            skArc(sketch, "E148.6", {"start": v(-214.4, -266.98) * mm, "mid": v(-217.67, -259.1) * mm, "end": v(-225.55, -255.83) * mm});
            skLineSegment(sketch, "E148.7", {"start": v(-229.16, -255.83) * mm, "end": v(-225.55, -255.83) * mm});
            skLineSegment(sketch, "E148.8", {"start": v(-229.16, -255.83) * mm, "end": v(-229.16, -242.55) * mm});
            skLineSegment(sketch, "E148.10", {"start": v(-242.2, -231.4) * mm, "end": v(-242.2, -215.82) * mm});
            skLineSegment(sketch, "E148.11", {"start": v(-242.2, -231.4) * mm, "end": v(-240.3, -231.4) * mm});
            skArc(sketch, "E148.12", {"start": v(-229.16, -242.55) * mm, "mid": v(-232.42, -234.66) * mm, "end": v(-240.3, -231.4) * mm});
            skLineSegment(sketch, "E148.13", {"start": v(-198.33, -297.8) * mm, "end": v(-198.33, -289.1) * mm});
            skLineSegment(sketch, "E148.14", {"start": v(-198.33, -297.8) * mm, "end": v(-192.5, -297.8) * mm});
            skArc(sketch, "E148.15", {"start": v(-181.36, -308.94) * mm, "mid": v(-184.62, -301.06) * mm, "end": v(-192.5, -297.8) * mm});
            skLineSegment(sketch, "E148.16", {"start": v(-181.36, -315.33) * mm, "end": v(-181.36, -308.94) * mm});
            skLineSegment(sketch, "E148.17", {"start": v(-181.36, -315.33) * mm, "end": v(-175.08, -315.33) * mm});
            skArc(sketch, "E148.18", {"start": v(-163.93, -326.48) * mm, "mid": v(-167.2, -318.6) * mm, "end": v(-175.08, -315.33) * mm});
            skLineSegment(sketch, "E148.19", {"start": v(-163.93, -330.57) * mm, "end": v(-163.93, -326.48) * mm});
            skLineSegment(sketch, "E148.20", {"start": v(-147.5, -330.57) * mm, "end": v(-163.93, -330.57) * mm});
            skArc(sketch, "E148.21", {"start": v(-132.25, -345.81) * mm, "mid": v(-136.72, -335.03) * mm, "end": v(-147.5, -330.57) * mm});
            skLineSegment(sketch, "E148.22", {"start": v(-132.25, -345.81) * mm, "end": v(-132.25, -348.99) * mm});
            skArc(sketch, "E148.23", {"start": v(-132.25, -348.99) * mm, "mid": v(-131.14, -351.68) * mm, "end": v(-128.44, -352.8) * mm});
            skLineSegment(sketch, "E148.24", {"start": v(-128.44, -352.8) * mm, "end": v(-98.32, -352.8) * mm});
            skLineSegment(sketch, "E149.0", {"start": v(-198.33, 55.8) * mm, "end": v(-198.33, 42.36) * mm});
            skArc(sketch, "E149.1", {"start": v(-209.48, 31.21) * mm, "mid": v(-201.6, 34.48) * mm, "end": v(-198.33, 42.36) * mm});
            skLineSegment(sketch, "E149.2", {"start": v(-214.4, 31.21) * mm, "end": v(-209.48, 31.21) * mm});
            skLineSegment(sketch, "E149.3", {"start": v(-214.4, 31.21) * mm, "end": v(-214.4, 20.23) * mm});
            skArc(sketch, "E149.4", {"start": v(-225.55, 9.08) * mm, "mid": v(-217.67, 12.34) * mm, "end": v(-214.4, 20.23) * mm});
            skLineSegment(sketch, "E149.5", {"start": v(-229.16, 9.08) * mm, "end": v(-225.55, 9.08) * mm});
            skLineSegment(sketch, "E149.6", {"start": v(-229.16, 9.08) * mm, "end": v(-229.16, -4.2) * mm});
            skArc(sketch, "E149.7", {"start": v(-240.3, -15.35) * mm, "mid": v(-232.42, -12.08) * mm, "end": v(-229.16, -4.2) * mm});
            skLineSegment(sketch, "E149.8", {"start": v(-242.2, -15.35) * mm, "end": v(-240.3, -15.35) * mm});
            skLineSegment(sketch, "E149.9", {"start": v(-242.2, -15.35) * mm, "end": v(-242.2, -30.93) * mm});
            skArc(sketch, "E149.10", {"start": v(-253.1, -42.07) * mm, "mid": v(-245.38, -38.72) * mm, "end": v(-242.2, -30.93) * mm});
            skLineSegment(sketch, "E149.11", {"start": v(-261.42, -176.02) * mm, "end": v(-261.42, -155.48) * mm});
            skArc(sketch, "E149.12", {"start": v(-253.1, -186.8) * mm, "mid": v(-255.42, -180) * mm, "end": v(-261.42, -176.02) * mm});
            skLineSegment(sketch, "E149.13", {"start": v(-253.1, -204.68) * mm, "end": v(-253.1, -186.8) * mm});
            skArc(sketch, "E149.14", {"start": v(-242.2, -215.82) * mm, "mid": v(-245.38, -208.03) * mm, "end": v(-253.1, -204.68) * mm});
            skArc(sketch, "E149.15", {"start": v(-261.42, -155.48) * mm, "mid": v(-262.85, -150.01) * mm, "end": v(-266.78, -145.95) * mm});
            skLineSegment(sketch, "E149.16", {"start": v(-266.78, -100.8) * mm, "end": v(-266.78, -145.95) * mm});
            skArc(sketch, "E149.17", {"start": v(-266.78, -100.8) * mm, "mid": v(-262.85, -96.74) * mm, "end": v(-261.42, -91.27) * mm});
            skLineSegment(sketch, "E149.18", {"start": v(-261.42, -70.73) * mm, "end": v(-261.42, -91.27) * mm});
            skArc(sketch, "E149.19", {"start": v(-261.42, -70.73) * mm, "mid": v(-255.42, -66.76) * mm, "end": v(-253.1, -59.95) * mm});
            skLineSegment(sketch, "E149.20", {"start": v(-253.1, -42.07) * mm, "end": v(-253.1, -59.95) * mm});
            skEllipticalArc(sketch, "E150.trimOffspring", {});
            skArc(sketch, "E151.1", {"start": v(-199.45, -12.2) * mm, "mid": v(-188, 2.25) * mm, "end": v(-183.92, 20.23) * mm});
            skArc(sketch, "E151.2", {"start": v(-211.88, -34.61) * mm, "mid": v(-203.9, -24.39) * mm, "end": v(-199.45, -12.2) * mm});
            skArc(sketch, "E151.3", {"start": v(-222.62, -59.02) * mm, "mid": v(-215.24, -47.7) * mm, "end": v(-211.88, -34.61) * mm});
            skLineSegment(sketch, "E151.4", {"start": v(-222.62, -59.02) * mm, "end": v(-222.62, -59.95) * mm});
            skArc(sketch, "E151.5", {"start": v(-230.94, -84.92) * mm, "mid": v(-224.76, -73.1) * mm, "end": v(-222.62, -59.95) * mm});
            skLineSegment(sketch, "E151.6", {"start": v(-230.94, -84.92) * mm, "end": v(-230.94, -91.27) * mm});
            skArc(sketch, "E151.7", {"start": v(-236.3, -111.7) * mm, "mid": v(-232.3, -101.83) * mm, "end": v(-230.94, -91.27) * mm});
            skLineSegment(sketch, "E151.8", {"start": v(253.83, -187.73) * mm, "end": v(253.83, -186.8) * mm});
            skArc(sketch, "E151.9", {"start": v(262.16, -161.83) * mm, "mid": v(255.97, -173.64) * mm, "end": v(253.83, -186.8) * mm});
            skLineSegment(sketch, "E151.10", {"start": v(262.16, -161.83) * mm, "end": v(262.16, -155.48) * mm});
            skArc(sketch, "E151.11", {"start": v(267.37, -135.3) * mm, "mid": v(263.48, -145.06) * mm, "end": v(262.16, -155.48) * mm});
            skLineSegment(sketch, "E151.12", {"start": v(267.37, -111.44) * mm, "end": v(267.37, -135.3) * mm});
            skArc(sketch, "E151.13", {"start": v(262.16, -91.27) * mm, "mid": v(263.48, -101.69) * mm, "end": v(267.37, -111.44) * mm});
            skLineSegment(sketch, "E151.14", {"start": v(262.16, -84.92) * mm, "end": v(262.16, -91.27) * mm});
            skArc(sketch, "E151.15", {"start": v(253.83, -59.95) * mm, "mid": v(255.97, -73.1) * mm, "end": v(262.16, -84.92) * mm});
            skLineSegment(sketch, "E151.16", {"start": v(253.83, -59.02) * mm, "end": v(253.83, -59.95) * mm});
            skArc(sketch, "E151.17", {"start": v(243.1, -34.61) * mm, "mid": v(246.46, -47.7) * mm, "end": v(253.83, -59.02) * mm});
            skArc(sketch, "E151.18", {"start": v(230.67, -12.2) * mm, "mid": v(235.11, -24.39) * mm, "end": v(243.1, -34.61) * mm});
            skArc(sketch, "E151.19", {"start": v(216.91, 8.2) * mm, "mid": v(222.25, -3.05) * mm, "end": v(230.67, -12.2) * mm});
            skArc(sketch, "E151.20", {"start": v(58.7, 172.32) * mm, "mid": v(42.14, 222) * mm, "end": v(4.48, 258.36) * mm});
            skArc(sketch, "E151.21", {"start": v(-74.64, 127.02) * mm, "mid": v(-28.98, 189.01) * mm, "end": v(4.48, 258.36) * mm});
            skArc(sketch, "E151.22", {"start": v(-132.57, 118.38) * mm, "mid": v(-102.04, 112.21) * mm, "end": v(-74.64, 127.02) * mm});
            skArc(sketch, "E151.23", {"start": v(-175.2, 35.96) * mm, "mid": v(-149.08, 74.7) * mm, "end": v(-132.57, 118.38) * mm});
            skArc(sketch, "E151.24", {"start": v(58.7, 172.32) * mm, "mid": v(88.7, 133.03) * mm, "end": v(136.9, 144) * mm});
            skArc(sketch, "E151.25", {"start": v(140.45, 147.4) * mm, "mid": v(138.65, 145.73) * mm, "end": v(136.9, 144) * mm});
            skArc(sketch, "E151.26", {"start": v(140.45, 147.4) * mm, "mid": v(148.5, 111.86) * mm, "end": v(164.67, 79.2) * mm});
            skArc(sketch, "E151.27", {"start": v(164.67, 79.2) * mm, "mid": v(170.76, 58.04) * mm, "end": v(186.8, 42.95) * mm});
            skArc(sketch, "E151.28", {"start": v(186.8, 42.95) * mm, "mid": v(193.36, 33.7) * mm, "end": v(202.17, 26.57) * mm});
            skArc(sketch, "E151.29", {"start": v(202.17, 26.57) * mm, "mid": v(208.21, 16.32) * mm, "end": v(216.91, 8.2) * mm});
            skArc(sketch, "E151.30", {"start": v(253.83, -187.73) * mm, "mid": v(246.46, -199.05) * mm, "end": v(243.1, -212.14) * mm});
            skArc(sketch, "E151.31", {"start": v(243.1, -212.14) * mm, "mid": v(235.11, -222.36) * mm, "end": v(230.67, -234.54) * mm});
            skArc(sketch, "E151.32", {"start": v(230.67, -234.54) * mm, "mid": v(222.25, -243.7) * mm, "end": v(216.91, -254.94) * mm});
            skArc(sketch, "E151.33", {"start": v(216.91, -254.94) * mm, "mid": v(208.21, -263.07) * mm, "end": v(202.17, -273.32) * mm});
            skArc(sketch, "E151.34", {"start": v(202.17, -273.32) * mm, "mid": v(193.36, -280.45) * mm, "end": v(186.8, -289.7) * mm});
            skArc(sketch, "E151.35", {"start": v(186.8, -289.7) * mm, "mid": v(179.93, -294.26) * mm, "end": v(174.1, -300.1) * mm});
            skArc(sketch, "E151.36", {"start": v(174.1, -300.1) * mm, "mid": v(151.84, -306.3) * mm, "end": v(135.45, -322.58) * mm});
            skLineSegment(sketch, "E151.37", {"start": v(132.85, -322.42) * mm, "end": v(135.45, -322.58) * mm});
            skArc(sketch, "E151.38", {"start": v(132.85, -322.42) * mm, "mid": v(104.31, -328.66) * mm, "end": v(83.34, -348.99) * mm});
            skLineSegment(sketch, "E151.39", {"start": v(-52.13, -348.99) * mm, "end": v(83.34, -348.99) * mm});
            skArc(sketch, "E151.40", {"start": v(-52.13, -348.99) * mm, "mid": v(-71.65, -329.46) * mm, "end": v(-98.32, -322.32) * mm});
            skLineSegment(sketch, "E151.41", {"start": v(-108.27, -322.32) * mm, "end": v(-98.32, -322.32) * mm});
            skArc(sketch, "E151.42", {"start": v(-108.27, -322.32) * mm, "mid": v(-122.89, -307.28) * mm, "end": v(-142.68, -300.34) * mm});
            skArc(sketch, "E151.43", {"start": v(-142.68, -300.34) * mm, "mid": v(-148.6, -294.36) * mm, "end": v(-155.6, -289.7) * mm});
            skArc(sketch, "E151.44", {"start": v(-155.6, -289.7) * mm, "mid": v(-162.15, -280.45) * mm, "end": v(-170.96, -273.32) * mm});
            skArc(sketch, "E151.45", {"start": v(-170.96, -273.32) * mm, "mid": v(-177, -263.07) * mm, "end": v(-185.7, -254.94) * mm});
            skArc(sketch, "E151.46", {"start": v(-185.7, -254.94) * mm, "mid": v(-191.04, -243.7) * mm, "end": v(-199.45, -234.54) * mm});
            skArc(sketch, "E151.47", {"start": v(-199.45, -234.54) * mm, "mid": v(-203.9, -222.36) * mm, "end": v(-211.88, -212.14) * mm});
            skArc(sketch, "E151.48", {"start": v(-211.88, -212.14) * mm, "mid": v(-215.24, -199.05) * mm, "end": v(-222.62, -187.73) * mm});
            skLineSegment(sketch, "E151.49", {"start": v(-222.62, -187.73) * mm, "end": v(-222.62, -186.8) * mm});
            skArc(sketch, "E151.50", {"start": v(-222.62, -186.8) * mm, "mid": v(-224.76, -173.64) * mm, "end": v(-230.94, -161.83) * mm});
            skLineSegment(sketch, "E151.51", {"start": v(-230.94, -161.83) * mm, "end": v(-230.94, -155.48) * mm});
            skArc(sketch, "E151.52", {"start": v(-230.94, -155.48) * mm, "mid": v(-232.3, -144.92) * mm, "end": v(-236.3, -135.05) * mm});
            skLineSegment(sketch, "E151.53", {"start": v(-236.3, -111.7) * mm, "end": v(-236.3, -135.05) * mm});
            skLineSegment(sketch, "E152", {"start": v(-183.92, 20.23) * mm, "end": v(-175.2, 35.96) * mm});
            skCircle(sketch, "E153", {"center": v(138.28, -185.3) * mm, "radius": 46.77 * mm});
            skCircle(sketch, "E154", {"center": v(-117.33, -179.54) * mm, "radius": 46.77 * mm});
            skCircle(sketch, "E155", {"center": v(138.28, -185.3) * mm, "radius": 11.49 * mm});
            skCircle(sketch, "E156", {"center": v(-117.33, -179.54) * mm, "radius": 11.49 * mm});
            skArc(sketch, "E157", {"start": v(49.28, -302.51) * mm, "mid": v(5.14, -288.09) * mm, "end": v(-40.08, -298.65) * mm});
            skArc(sketch, "E158", {"start": v(47.75, -313.8) * mm, "mid": v(7.22, -311.6) * mm, "end": v(-33.33, -313.54) * mm});
            skArc(sketch, "E159", {"start": v(-43.37, -303.9) * mm, "mid": v(-40.55, -311) * mm, "end": v(-33.33, -313.54) * mm});
            skArc(sketch, "E160", {"start": v(49.84, -313.04) * mm, "mid": v(51.06, -311.42) * mm, "end": v(51.86, -309.55) * mm});
            skPoint(sketch, "E161.visualSharp", {"position": v(-42.2, -299.85) * mm});
            skArc(sketch, "E161.filletArc", {"start": v(-40.08, -298.65) * mm, "mid": v(-42.4, -300.84) * mm, "end": v(-43.37, -303.9) * mm});
            skPoint(sketch, "E162.visualSharp", {"position": v(51.56, -304.08) * mm});
            skArc(sketch, "E162.filletArc", {"start": v(51.86, -309.55) * mm, "mid": v(51.72, -305.6) * mm, "end": v(49.28, -302.51) * mm});
            skPoint(sketch, "E163.visualSharp", {"position": v(48.84, -313.91) * mm});
            skArc(sketch, "E163.filletArc", {"start": v(47.75, -313.8) * mm, "mid": v(48.88, -313.66) * mm, "end": v(49.84, -313.04) * mm});
            skArc(sketch, "E164", {"start": v(48.44, 262.65) * mm, "mid": v(74.23, 331.18) * mm, "end": v(15.94, 286.87) * mm});
            skArc(sketch, "E165", {"start": v(50.3, 271.45) * mm, "mid": v(68.92, 324.05) * mm, "end": v(23.83, 291.18) * mm});
            const initialGuessF0  = {"E0": [0.015606262721121311, -0.12337441742420203, 1, 0, 0.2913808896674736, 0.28027729201028595, 2.4269216203888186, 0.8763435288441446], "E150.trimOffspring": [0.015606262721121311, -0.12337441742420203, 1, 0, 0.2913808896674736, 0.28027729201028595, 0.9507688842144981, 2.2936118672603896]};
            skSetInitialGuess(sketch, initialGuessF0);
            skSolve(sketch);
        }
        {
            var Q0;
            Q0=makeQuery(id+"F0.imprint","IMPRINT",FACE,{"disambiguationData":[TD([[makeQuery(id+"F0.imprint","IMPRINT",EDGE,{"derivedFrom":sQuery(id+"F0.wireOp",EDGE,"E144.1")}),-1.0]])]});
            var Q1;
            {var subQ0=sQuery(id+"F0.wireOp",EDGE,"E144.18");Q1=makeQuery(id+"F0.imprint","IMPRINT",FACE,{"disambiguationData":[TD([[makeQuery(id+"F0.imprint","IMPRINT",EDGE,{"derivedFrom":subQ0}),1.0]])]});}
            var Q2;
            {var subQ0=sQuery(id+"F0.wireOp",EDGE,"E151.21");var subQ1=sQuery(id+"F0.wireOp",EDGE,"E150.trimOffspring");var subQ2=makeQuery(id+"F0.imprint","INTERSECT",VERTEX,{"derivedFrom":[subQ1,subQ0]});Q2=makeQuery(id+"F0.imprint","IMPRINT",FACE,{"disambiguationData":[TD([[makeQuery(id+"F0.imprint","IMPRINT",EDGE,{"disambiguationData":[TD([[subQ2,-1.0]])],"derivedFrom":subQ1}),1.0]])]});}
            var Q3;
            {var subQ0=sQuery(id+"F0.wireOp",EDGE,"E151.24");var subQ1=sQuery(id+"F0.wireOp",EDGE,"E150.trimOffspring");var subQ2=makeQuery(id+"F0.imprint","INTERSECT",VERTEX,{"disambiguationData":[OD(0.0)],"derivedFrom":[subQ1,subQ0]});Q3=makeQuery(id+"F0.imprint","IMPRINT",FACE,{"disambiguationData":[TD([[makeQuery(id+"F0.imprint","IMPRINT",EDGE,{"disambiguationData":[TD([[subQ2,-1.0]])],"derivedFrom":subQ1}),1.0]])]});}
            extrude(context, id + "F1", {"entities" : qUnion([Q0, Q1, Q2, Q3]), "depth" : 88.9 * mm});
        }
        {
            var Q0;
            Q0=makeQuery(id+"F0.imprint","IMPRINT",FACE,{"disambiguationData":[TD([[makeQuery(id+"F0.imprint","IMPRINT",EDGE,{"derivedFrom":sQuery(id+"F0.wireOp",EDGE,"E1")}),-1.0]])]});
            var Q1;
            {var subQ0=sQuery(id+"F0.wireOp",EDGE,"E165");var subQ1=sQuery(id+"F0.wireOp",EDGE,"E2");var subQ8=makeQuery(id+"F0.imprint","INTERSECT",VERTEX,{"disambiguationData":[OD(0.0)],"derivedFrom":[subQ1,subQ0]});Q1=makeQuery(id+"F0.imprint","IMPRINT",FACE,{"disambiguationData":[TD([[makeQuery(id+"F0.imprint","IMPRINT",EDGE,{"disambiguationData":[TD([[subQ8,1.0]])],"derivedFrom":subQ1}),1.0]])]});}
            var Q2;
            {var subQ0=sQuery(id+"F0.wireOp",EDGE,"E165");Q2=makeQuery(id+"F0.imprint","IMPRINT",FACE,{"disambiguationData":[TD([[makeQuery(id+"F0.imprint","IMPRINT",EDGE,{"derivedFrom":subQ0}),-1.0]])]});}
            extrude(context, id + "F2", {"entities" : qUnion([Q0, Q1, Q2]), "depth" : 114.3 * mm});
        }
        {
            var Q0;
            Q0=makeQuery(id+"F0.imprint","IMPRINT",FACE,{"disambiguationData":[TD([[makeQuery(id+"F0.imprint","IMPRINT",EDGE,{"derivedFrom":sQuery(id+"F0.wireOp",EDGE,"E1")}),-1.0]])]});
            var Q1;
            {var subQ0=sQuery(id+"F0.wireOp",EDGE,"E165");var subQ1=sQuery(id+"F0.wireOp",EDGE,"E2");var subQ8=makeQuery(id+"F0.imprint","INTERSECT",VERTEX,{"disambiguationData":[OD(0.0)],"derivedFrom":[subQ1,subQ0]});Q1=makeQuery(id+"F0.imprint","IMPRINT",FACE,{"disambiguationData":[TD([[makeQuery(id+"F0.imprint","IMPRINT",EDGE,{"disambiguationData":[TD([[subQ8,1.0]])],"derivedFrom":subQ1}),1.0]])]});}
            var Q2;
            {var subQ0=sQuery(id+"F0.wireOp",EDGE,"E165");Q2=makeQuery(id+"F0.imprint","IMPRINT",FACE,{"disambiguationData":[TD([[makeQuery(id+"F0.imprint","IMPRINT",EDGE,{"derivedFrom":subQ0}),-1.0]])]});}
            extrude(context, id + "F3", {"entities" : qUnion([Q0, Q1, Q2]), "operationType" : NewBodyOperationType.ADD, "oppositeDirection" : true, "depth" : 114.3 * mm});
        }
        {
            var Q0;
            Q0=makeQuery(id+"F0.imprint","IMPRINT",FACE,{"disambiguationData":[TD([[makeQuery(id+"F0.imprint","IMPRINT",EDGE,{"derivedFrom":sQuery(id+"F0.wireOp",EDGE,"E144.1")}),-1.0]])]});
            var Q1;
            {var subQ5=sQuery(id+"F0.wireOp",EDGE,"E144.18");Q1=makeQuery(id+"F0.imprint","IMPRINT",FACE,{"disambiguationData":[TD([[makeQuery(id+"F0.imprint","IMPRINT",EDGE,{"derivedFrom":subQ5}),1.0]])]});}
            var Q2;
            {var subQ0=sQuery(id+"F0.wireOp",EDGE,"E151.24");var subQ1=sQuery(id+"F0.wireOp",EDGE,"E150.trimOffspring");var subQ2=makeQuery(id+"F0.imprint","INTERSECT",VERTEX,{"disambiguationData":[OD(0.0)],"derivedFrom":[subQ1,subQ0]});Q2=makeQuery(id+"F0.imprint","IMPRINT",FACE,{"disambiguationData":[TD([[makeQuery(id+"F0.imprint","IMPRINT",EDGE,{"disambiguationData":[TD([[subQ2,-1.0]])],"derivedFrom":subQ1}),1.0]])]});}
            var Q3;
            {var subQ0=sQuery(id+"F0.wireOp",EDGE,"E151.21");var subQ1=sQuery(id+"F0.wireOp",EDGE,"E150.trimOffspring");var subQ2=makeQuery(id+"F0.imprint","INTERSECT",VERTEX,{"derivedFrom":[subQ1,subQ0]});Q3=makeQuery(id+"F0.imprint","IMPRINT",FACE,{"disambiguationData":[TD([[makeQuery(id+"F0.imprint","IMPRINT",EDGE,{"disambiguationData":[TD([[subQ2,-1.0]])],"derivedFrom":subQ1}),1.0]])]});}
            extrude(context, id + "F4", {"entities" : qUnion([Q0, Q1, Q2, Q3]), "oppositeDirection" : true, "depth" : 88.9 * mm});
        }
        {
            var Q0;
            Q0=makeQuery(id+"F0.imprint","IMPRINT",FACE,{"disambiguationData":[TD([[makeQuery(id+"F0.imprint","IMPRINT",EDGE,{"derivedFrom":sQuery(id+"F0.wireOp",EDGE,"E151.1")}),-1.0]])]});
            var Q1;
            {var subQ5=sQuery(id+"F0.wireOp",EDGE,"E151.20");Q1=makeQuery(id+"F0.imprint","IMPRINT",FACE,{"disambiguationData":[TD([[makeQuery(id+"F0.imprint","IMPRINT",EDGE,{"derivedFrom":subQ5}),1.0]])]});}
            var Q2;
            {var subQ5=sQuery(id+"F0.wireOp",EDGE,"E151.25");Q2=makeQuery(id+"F0.imprint","IMPRINT",FACE,{"disambiguationData":[TD([[makeQuery(id+"F0.imprint","IMPRINT",EDGE,{"derivedFrom":subQ5}),1.0]])]});}
            var Q3;
            Q3=makeQuery(id+"F0.imprint","IMPRINT",FACE,{"disambiguationData":[TD([[makeQuery(id+"F0.imprint","IMPRINT",EDGE,{"derivedFrom":sQuery(id+"F0.wireOp",EDGE,"E156")}),1.0]])]});
            var Q4;
            Q4=makeQuery(id+"F0.imprint","IMPRINT",FACE,{"disambiguationData":[TD([[makeQuery(id+"F0.imprint","IMPRINT",EDGE,{"derivedFrom":sQuery(id+"F0.wireOp",EDGE,"E155")}),1.0]])]});
            extrude(context, id + "F5", {"entities" : qUnion([Q0, Q1, Q2, Q3, Q4]), "operationType" : NewBodyOperationType.ADD, "depth" : 66.04 * mm});
        }
        {
            var Q0;
            Q0=makeQuery(id+"F0.imprint","IMPRINT",FACE,{"disambiguationData":[TD([[makeQuery(id+"F0.imprint","IMPRINT",EDGE,{"derivedFrom":sQuery(id+"F0.wireOp",EDGE,"E151.1")}),-1.0]])]});
            var Q1;
            {var subQ5=sQuery(id+"F0.wireOp",EDGE,"E151.25");Q1=makeQuery(id+"F0.imprint","IMPRINT",FACE,{"disambiguationData":[TD([[makeQuery(id+"F0.imprint","IMPRINT",EDGE,{"derivedFrom":subQ5}),1.0]])]});}
            var Q2;
            {var subQ5=sQuery(id+"F0.wireOp",EDGE,"E151.20");Q2=makeQuery(id+"F0.imprint","IMPRINT",FACE,{"disambiguationData":[TD([[makeQuery(id+"F0.imprint","IMPRINT",EDGE,{"derivedFrom":subQ5}),1.0]])]});}
            var Q3;
            Q3=makeQuery(id+"F0.imprint","IMPRINT",FACE,{"disambiguationData":[TD([[makeQuery(id+"F0.imprint","IMPRINT",EDGE,{"derivedFrom":sQuery(id+"F0.wireOp",EDGE,"E154")}),1.0]])]});
            var Q4;
            Q4=makeQuery(id+"F0.imprint","IMPRINT",FACE,{"disambiguationData":[TD([[makeQuery(id+"F0.imprint","IMPRINT",EDGE,{"derivedFrom":sQuery(id+"F0.wireOp",EDGE,"E157")}),1.0]])]});
            var Q5;
            Q5=makeQuery(id+"F0.imprint","IMPRINT",FACE,{"disambiguationData":[TD([[makeQuery(id+"F0.imprint","IMPRINT",EDGE,{"derivedFrom":sQuery(id+"F0.wireOp",EDGE,"E153")}),1.0]])]});
            extrude(context, id + "F6", {"entities" : qUnion([Q0, Q1, Q2, Q3, Q4, Q5]), "operationType" : NewBodyOperationType.ADD, "oppositeDirection" : true, "depth" : 66.04 * mm});
        }
        {
            var Q0;
            Q0=makeQuery(id+"F0.imprint","IMPRINT",FACE,{"disambiguationData":[TD([[makeQuery(id+"F0.imprint","IMPRINT",EDGE,{"derivedFrom":sQuery(id+"F0.wireOp",EDGE,"E153")}),1.0]])]});
            var Q1;
            Q1=makeQuery(id+"F0.imprint","IMPRINT",FACE,{"disambiguationData":[TD([[makeQuery(id+"F0.imprint","IMPRINT",EDGE,{"derivedFrom":sQuery(id+"F0.wireOp",EDGE,"E154")}),1.0]])]});
            var Q2;
            Q2=makeQuery(id+"F0.imprint","IMPRINT",FACE,{"disambiguationData":[TD([[makeQuery(id+"F0.imprint","IMPRINT",EDGE,{"derivedFrom":sQuery(id+"F0.wireOp",EDGE,"E157")}),1.0]])]});
            extrude(context, id + "F7", {"entities" : qUnion([Q0, Q1, Q2]), "depth" : 54.6 * mm});
        }
        {
            var Q0;
            Q0=makeQuery(id+"F0.imprint","IMPRINT",FACE,{"disambiguationData":[TD([[makeQuery(id+"F0.imprint","IMPRINT",EDGE,{"derivedFrom":sQuery(id+"F0.wireOp",EDGE,"E156")}),1.0]])]});
            var Q1;
            Q1=makeQuery(id+"F0.imprint","IMPRINT",FACE,{"disambiguationData":[TD([[makeQuery(id+"F0.imprint","IMPRINT",EDGE,{"derivedFrom":sQuery(id+"F0.wireOp",EDGE,"E155")}),1.0]])]});
            extrude(context, id + "F8", {"entities" : qUnion([Q0, Q1]), "oppositeDirection" : true, "depth" : 66.04 * mm});
        }
    });
